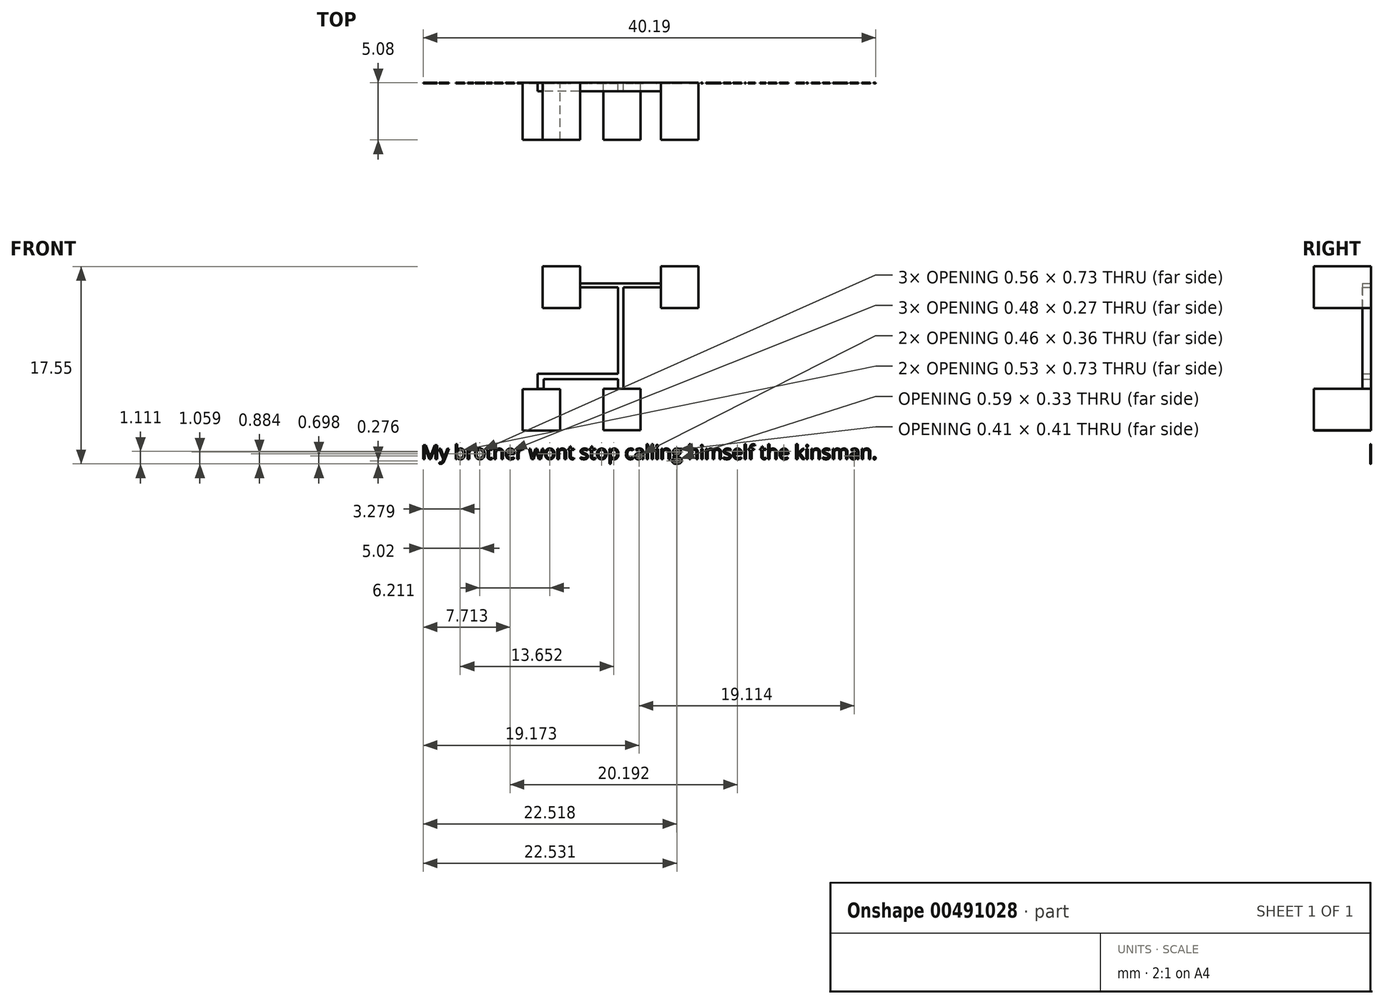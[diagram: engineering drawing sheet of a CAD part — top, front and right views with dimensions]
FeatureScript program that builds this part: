
annotation { "Feature Type Name" : "Feature", "Feature Type Description" : "" }
export const myFeature = defineFeature(function(context is Context, id is Id, definition is map)
    precondition{}
    {
        {
            var Q0;
            Q0=qCreatedBy(makeId("Front.planeOp"),FACE);
            var sketch = newSketch(context, id + "F0", { "sketchPlane" : qUnion([Q0])});
            skLineSegment(sketch, "E0.bottom", {"start": v(-33.92, 38.53) * mm, "end": v(-30.6, 38.53) * mm});
            skLineSegment(sketch, "E0.top", {"start": v(-33.92, 34.84) * mm, "end": v(-30.6, 34.84) * mm});
            skLineSegment(sketch, "E0.left", {"start": v(-33.92, 38.53) * mm, "end": v(-33.92, 34.84) * mm});
            skLineSegment(sketch, "E0.right", {"start": v(-30.6, 38.53) * mm, "end": v(-30.6, 34.84) * mm});
            skLineSegment(sketch, "E1", {"start": v(-30.6, 36.69) * mm, "end": v(-23.41, 36.69) * mm});
            skLineSegment(sketch, "E2.bottom", {"start": v(-23.41, 38.53) * mm, "end": v(-20.1, 38.53) * mm});
            skLineSegment(sketch, "E2.top", {"start": v(-23.41, 34.84) * mm, "end": v(-20.1, 34.84) * mm});
            skLineSegment(sketch, "E2.left", {"start": v(-23.41, 38.53) * mm, "end": v(-23.41, 34.84) * mm});
            skLineSegment(sketch, "E2.right", {"start": v(-20.1, 38.53) * mm, "end": v(-20.1, 34.84) * mm});
            skLineSegment(sketch, "E3", {"start": v(-30.6, 37.04) * mm, "end": v(-23.41, 37.04) * mm});
            skLineSegment(sketch, "E4", {"start": v(-27.24, 36.69) * mm, "end": v(-27.24, 27.67) * mm});
            skLineSegment(sketch, "E5", {"start": v(-27.24, 27.67) * mm, "end": v(-27, 27.67) * mm});
            skLineSegment(sketch, "E6", {"start": v(-27, 27.67) * mm, "end": v(-26.77, 27.67) * mm});
            skLineSegment(sketch, "E7", {"start": v(-26.77, 27.67) * mm, "end": v(-26.77, 36.69) * mm});
            skLineSegment(sketch, "E8.bottom", {"start": v(-28.54, 27.67) * mm, "end": v(-25.22, 27.67) * mm});
            skLineSegment(sketch, "E8.top", {"start": v(-28.54, 23.98) * mm, "end": v(-25.22, 23.98) * mm});
            skLineSegment(sketch, "E8.left", {"start": v(-28.54, 27.67) * mm, "end": v(-28.54, 23.98) * mm});
            skLineSegment(sketch, "E8.right", {"start": v(-25.22, 27.67) * mm, "end": v(-25.22, 23.98) * mm});
            skLineSegment(sketch, "E9", {"start": v(-27.24, 28.52) * mm, "end": v(-32.45, 28.52) * mm});
            skLineSegment(sketch, "E10", {"start": v(-32.45, 28.52) * mm, "end": v(-34.39, 28.52) * mm});
            skLineSegment(sketch, "E11", {"start": v(-34.39, 28.52) * mm, "end": v(-34.39, 28.99) * mm});
            skLineSegment(sketch, "E12", {"start": v(-34.39, 28.99) * mm, "end": v(-27.24, 28.99) * mm});
            skLineSegment(sketch, "E13", {"start": v(-34.39, 28.52) * mm, "end": v(-34.39, 27.67) * mm});
            skLineSegment(sketch, "E14", {"start": v(-27.24, 27.67) * mm, "end": v(-27.24, 28.52) * mm});
            skLineSegment(sketch, "E15", {"start": v(-34.39, 27.67) * mm, "end": v(-33.85, 27.67) * mm});
            skLineSegment(sketch, "E16", {"start": v(-33.85, 27.67) * mm, "end": v(-33.85, 28.52) * mm});
            skLineSegment(sketch, "E17.bottom", {"start": v(-35.7, 27.63) * mm, "end": v(-32.39, 27.63) * mm});
            skLineSegment(sketch, "E17.top", {"start": v(-35.7, 23.94) * mm, "end": v(-32.39, 23.94) * mm});
            skLineSegment(sketch, "E17.left", {"start": v(-35.7, 27.63) * mm, "end": v(-35.7, 23.94) * mm});
            skLineSegment(sketch, "E17.right", {"start": v(-32.39, 27.63) * mm, "end": v(-32.39, 23.94) * mm});
            skSolve(sketch);
        }
        {
            var Q0;
            {var subQ3=sQuery(id+"F0.wireOp",EDGE,"E2.bottom");Q0=makeQuery(id+"F0.imprint","IMPRINT",FACE,{"disambiguationData":[TD([[makeQuery(id+"F0.imprint","IMPRINT",EDGE,{"derivedFrom":subQ3}),-1.0]])]});}
            var Q1;
            Q1=makeQuery(id+"F0.imprint","IMPRINT",FACE,{"disambiguationData":[TD([[makeQuery(id+"F0.imprint","IMPRINT",EDGE,{"derivedFrom":sQuery(id+"F0.wireOp",EDGE,"E8.top")}),1.0]])]});
            var Q2;
            Q2=makeQuery(id+"F0.imprint","IMPRINT",FACE,{"disambiguationData":[TD([[makeQuery(id+"F0.imprint","IMPRINT",EDGE,{"derivedFrom":sQuery(id+"F0.wireOp",EDGE,"E17.bottom")}),-1.0]])]});
            var Q3;
            {var subQ1=sQuery(id+"F0.wireOp",EDGE,"E0.bottom");Q3=makeQuery(id+"F0.imprint","IMPRINT",FACE,{"disambiguationData":[TD([[makeQuery(id+"F0.imprint","IMPRINT",EDGE,{"derivedFrom":subQ1}),-1.0]])]});}
            extrude(context, id + "F1", {"entities" : qUnion([Q0, Q1, Q2, Q3]), "depth" : 5.08 * mm});
        }
        {
            var Q0;
            {var subQ7=sQuery(id+"F0.wireOp",EDGE,"E3");Q0=makeQuery(id+"F0.imprint","IMPRINT",FACE,{"disambiguationData":[TD([[makeQuery(id+"F0.imprint","IMPRINT",EDGE,{"derivedFrom":subQ7}),-1.0]])]});}
            var Q1;
            {var subQ0=sQuery(id+"F0.wireOp",EDGE,"E7");Q1=makeQuery(id+"F0.imprint","IMPRINT",FACE,{"disambiguationData":[TD([[makeQuery(id+"F0.imprint","IMPRINT",EDGE,{"derivedFrom":subQ0}),1.0]])]});}
            var Q2;
            {var subQ1=sQuery(id+"F0.wireOp",EDGE,"E9");Q2=makeQuery(id+"F0.imprint","IMPRINT",FACE,{"disambiguationData":[TD([[makeQuery(id+"F0.imprint","IMPRINT",EDGE,{"derivedFrom":subQ1}),-1.0]])]});}
            var Q3;
            {var subQ0=sQuery(id+"F0.wireOp",EDGE,"E13");Q3=makeQuery(id+"F0.imprint","IMPRINT",FACE,{"disambiguationData":[TD([[makeQuery(id+"F0.imprint","IMPRINT",EDGE,{"derivedFrom":subQ0}),1.0]])]});}
            extrude(context, id + "F2", {"entities" : qUnion([Q0, Q1, Q2, Q3]), "depth" : 0.76 * mm});
        }
        {
            var Q0;
            Q0=qCreatedBy(makeId("Front.planeOp"),FACE);
            var sketch = newSketch(context, id + "F3", { "sketchPlane" : qUnion([Q0])});
            skText(sketch, "E18", { "text": "My brother wont stop calling himself the kinsman.\n", "fontName": "OpenSans-Regular.ttf"});
            const initialGuessF3  = {"E18": [-0.0447, 0.0214, 1, 0, 0.00125]};
            skSetInitialGuess(sketch, initialGuessF3);
            skSolve(sketch);
        }
        {
            var Q0;
            Q0 = qSketchRegion(id + "F3", true);
            extrude(context, id + "F4", {"entities" : qUnion([Q0]), "depth" : 0.05 * mm});
        }
    });
